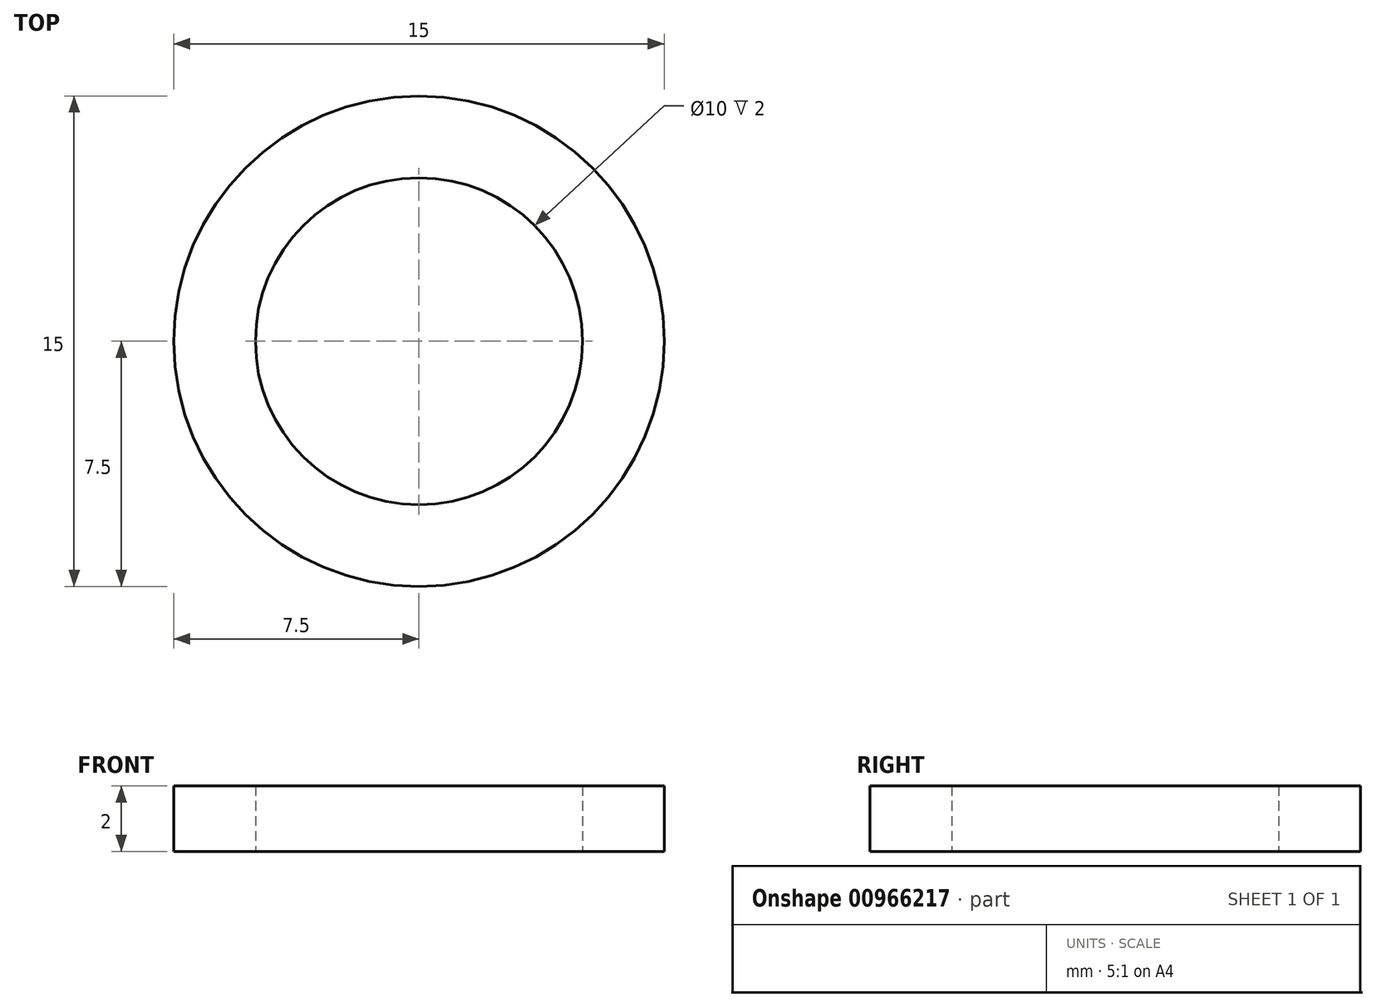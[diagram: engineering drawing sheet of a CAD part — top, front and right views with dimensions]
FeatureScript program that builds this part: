
annotation { "Feature Type Name" : "Feature", "Feature Type Description" : "" }
export const myFeature = defineFeature(function(context is Context, id is Id, definition is map)
    precondition{}
    {
        {
            var Q0;
            Q0=qCreatedBy(makeId("Top.planeOp"),FACE);
            var sketch = newSketch(context, id + "F0", { "sketchPlane" : qUnion([Q0])});
            skCircle(sketch, "E0", {"center": v(0, 0) * mm, "radius": 5 * mm});
            skCircle(sketch, "E1", {"center": v(0, 0) * mm, "radius": 7.5 * mm});
            skSolve(sketch);
        }
        {
            var Q0;
            Q0=makeQuery(id+"F0.imprint","IMPRINT",FACE,{"disambiguationData":[TD([[makeQuery(id+"F0.imprint","IMPRINT",EDGE,{"derivedFrom":sQuery(id+"F0.wireOp",EDGE,"E0")}),-1.0]])]});
            extrude(context, id + "F1", {"entities" : qUnion([Q0]), "depth" : 2 * mm, "offsetDistance" : 25 * mm});
        }
    });
